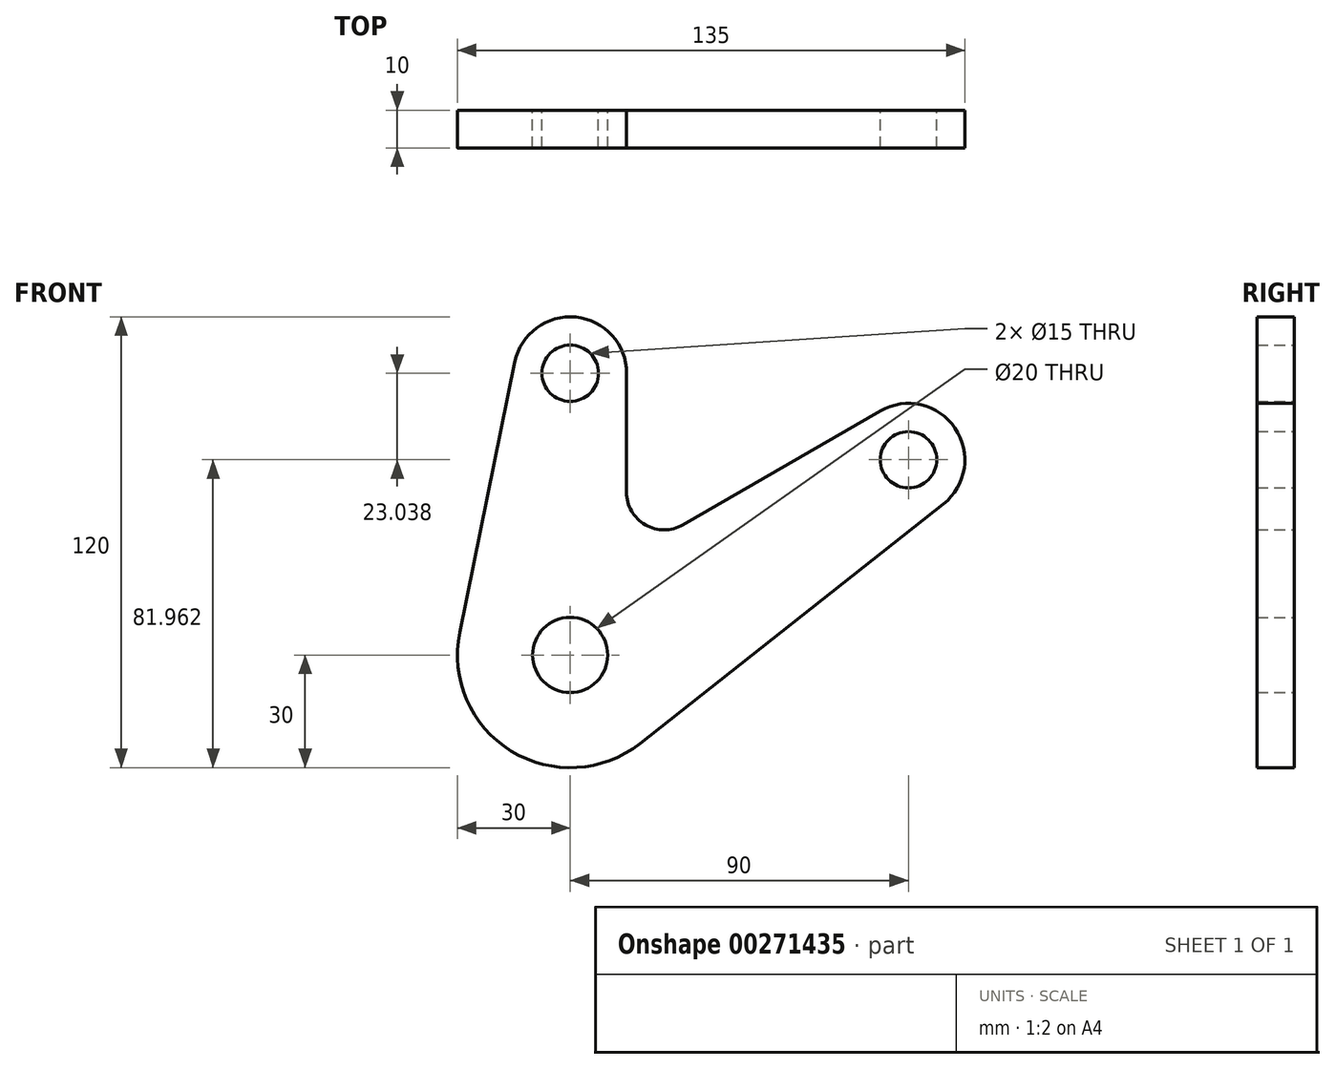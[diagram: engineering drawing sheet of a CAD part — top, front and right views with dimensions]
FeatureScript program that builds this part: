
annotation { "Feature Type Name" : "Feature", "Feature Type Description" : "" }
export const myFeature = defineFeature(function(context is Context, id is Id, definition is map)
    precondition{}
    {
        {
            var Q0;
            Q0=qCreatedBy(makeId("Front.planeOp"),FACE);
            var sketch = newSketch(context, id + "F0", { "sketchPlane" : qUnion([Q0])});
            skCircle(sketch, "E0", {"center": v(0, 0) * mm, "radius": 10 * mm});
            skLineSegment(sketch, "E1", {"start": v(18.6, -23.54) * mm, "end": v(99.3, 40.19) * mm});
            skArc(sketch, "E2", {"start": v(-29.4, 6) * mm, "mid": v(-15.73, -25.55) * mm, "end": v(18.6, -23.54) * mm});
            skLineSegment(sketch, "E3", {"start": v(-29.4, 6) * mm, "end": v(-14.7, 78) * mm});
            skLineSegment(sketch, "E4", {"start": v(82.5, 64.95) * mm, "end": v(30, 34.64) * mm});
            skLineSegment(sketch, "E5", {"start": v(15, 43.3) * mm, "end": v(15, 75) * mm});
            skArc(sketch, "E6", {"start": v(15, 43.3) * mm, "mid": v(20, 34.64) * mm, "end": v(30, 34.64) * mm});
            skArc(sketch, "E7", {"start": v(15, 75) * mm, "mid": v(1.5, 89.92) * mm, "end": v(-14.7, 78) * mm});
            skArc(sketch, "E8", {"start": v(99.3, 40.19) * mm, "mid": v(102.41, 60.38) * mm, "end": v(82.5, 64.95) * mm});
            skLineSegment(sketch, "E9", {"start": v(0, 75) * mm, "end": v(0, 0) * mm, "construction": true});
            skLineSegment(sketch, "E10", {"start": v(90, 51.96) * mm, "end": v(0, 0) * mm, "construction": true});
            skCircle(sketch, "E11", {"center": v(0, 75) * mm, "radius": 7.5 * mm});
            skCircle(sketch, "E12", {"center": v(90, 51.96) * mm, "radius": 7.5 * mm});
            skSolve(sketch);
        }
        {
            var Q0;
            Q0 = qSketchRegion(id + "F0", true);
            extrude(context, id + "F1", {"entities" : qUnion([Q0]), "depth" : 10 * mm});
        }
    });
